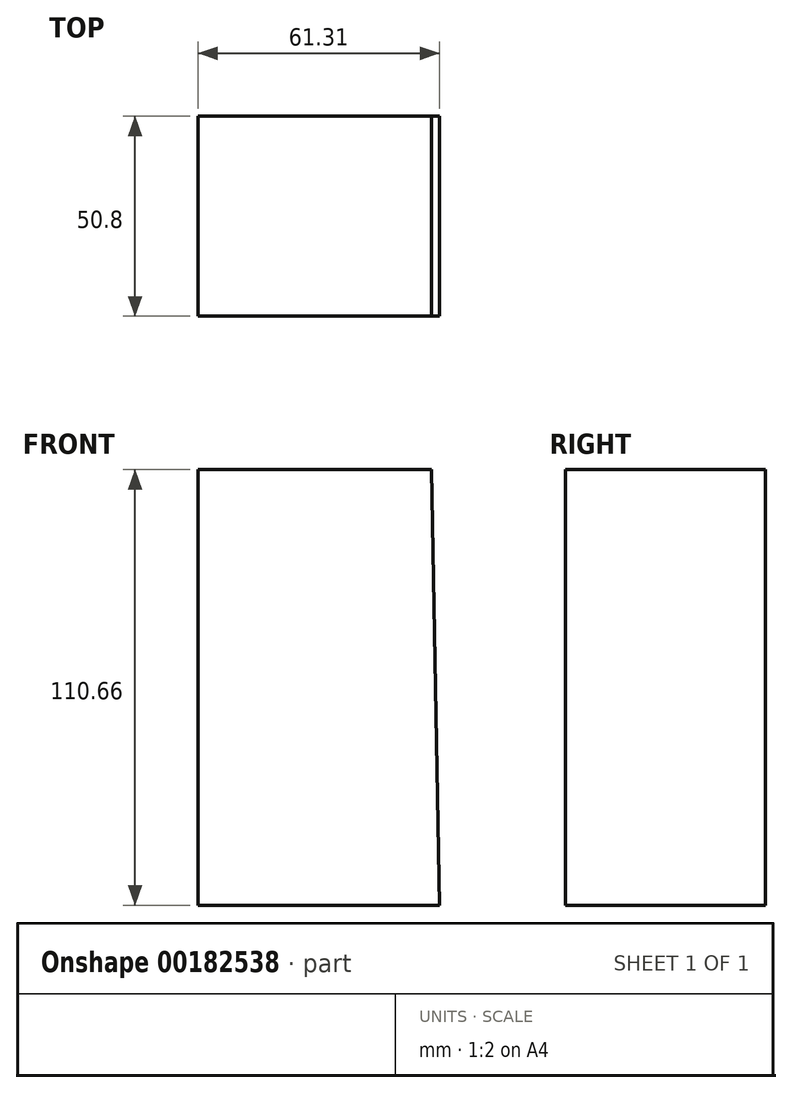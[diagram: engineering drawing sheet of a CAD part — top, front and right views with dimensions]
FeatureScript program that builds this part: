
annotation { "Feature Type Name" : "Feature", "Feature Type Description" : "" }
export const myFeature = defineFeature(function(context is Context, id is Id, definition is map)
    precondition{}
    {
        {
            var Q0;
            Q0=qCreatedBy(makeId("Front.planeOp"),FACE);
            var sketch = newSketch(context, id + "F0", { "sketchPlane" : qUnion([Q0])});
            skLineSegment(sketch, "E0", {"start": v(-14.3, 43.19) * mm, "end": v(45.05, 43.19) * mm});
            skLineSegment(sketch, "E1", {"start": v(45.05, 43.19) * mm, "end": v(47, -67.47) * mm});
            skLineSegment(sketch, "E2", {"start": v(-14.3, 43.19) * mm, "end": v(-14.3, -67.47) * mm});
            skLineSegment(sketch, "E3", {"start": v(-14.3, -67.47) * mm, "end": v(47, -67.47) * mm});
            skSolve(sketch);
        }
        {
            var Q0;
            Q0=makeQuery(id+"F0.imprint","IMPRINT",FACE,{"disambiguationData":[TD([[makeQuery(id+"F0.imprint","IMPRINT",EDGE,{"derivedFrom":sQuery(id+"F0.wireOp",EDGE,"E0")}),-1.0]])]});
            extrude(context, id + "F1", {"entities" : qUnion([Q0]), "depth" : 50.8 * mm});
        }
    });
